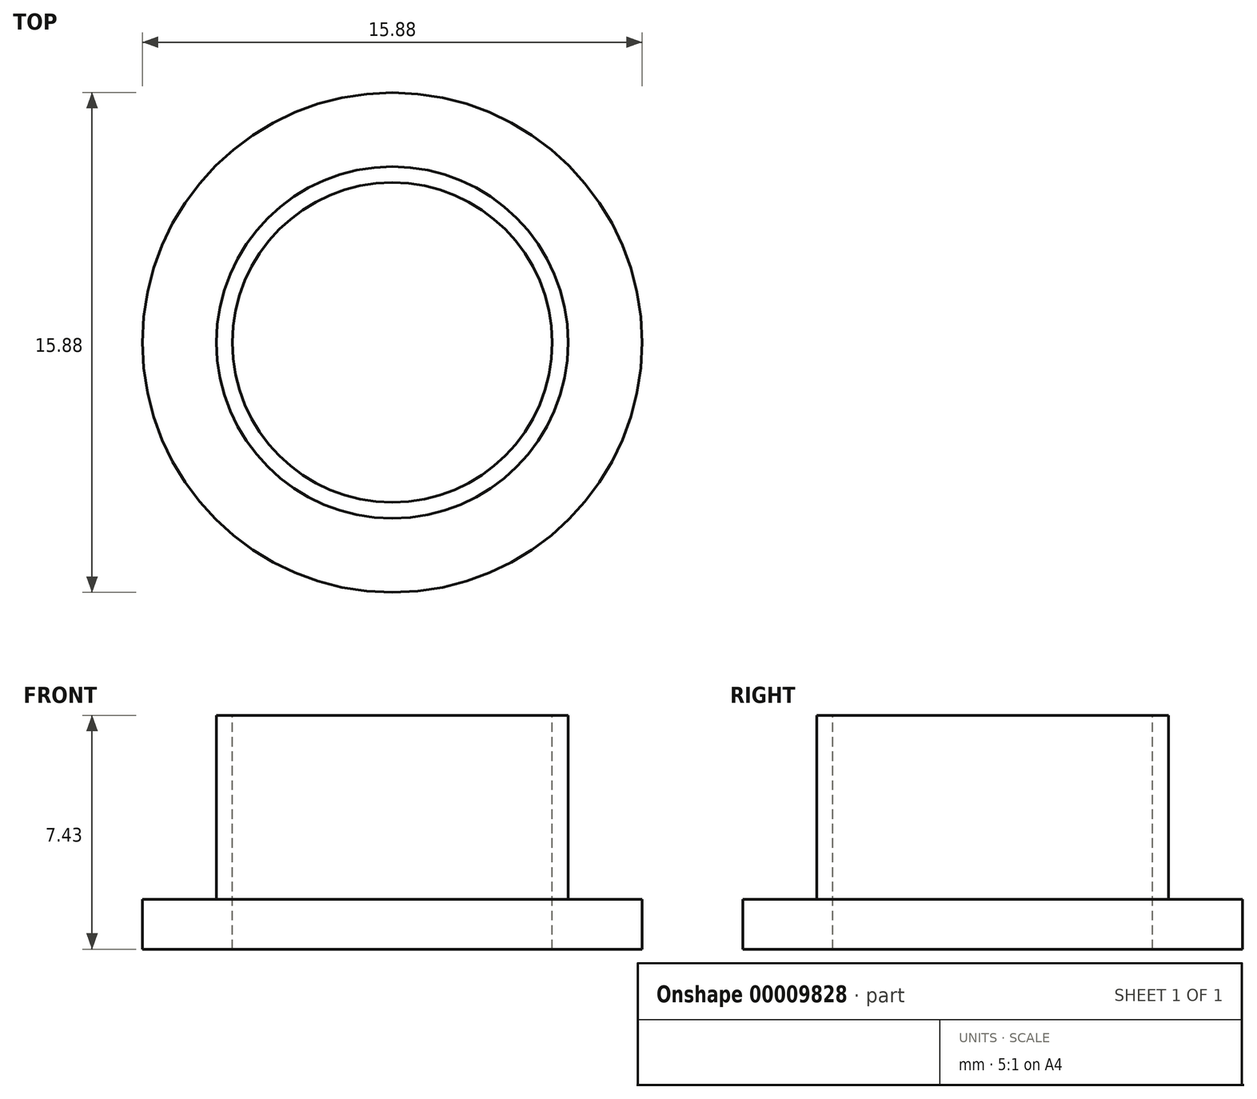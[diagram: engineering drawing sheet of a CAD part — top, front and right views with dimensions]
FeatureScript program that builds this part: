
annotation { "Feature Type Name" : "Feature", "Feature Type Description" : "" }
export const myFeature = defineFeature(function(context is Context, id is Id, definition is map)
    precondition{}
    {
        {
            var Q0;
            Q0=qCreatedBy(makeId("Top.planeOp"),FACE);
            var sketch = newSketch(context, id + "F0", { "sketchPlane" : qUnion([Q0])});
            skCircle(sketch, "E0", {"center": v(0, 0) * mm, "radius": 7.94 * mm});
            skSolve(sketch);
        }
        {
            var Q0;
            Q0=makeQuery(id+"F0.imprint","IMPRINT",FACE,{"disambiguationData":[TD([[makeQuery(id+"F0.imprint","IMPRINT",EDGE,{"derivedFrom":sQuery(id+"F0.wireOp",EDGE,"E0")}),1.0]])]});
            extrude(context, id + "F1", {"entities" : qUnion([Q0]), "depth" : 1.59 * mm});
        }
        {
            var Q0;
            Q0=makeQuery(id+"F1.opExtrude","CAP_FACE",FACE,{"disambiguationData":[OSD([sQuery(id+"F0.wireOp",EDGE,"E0")])],"isStart":false});
            var sketch = newSketch(context, id + "F2", { "sketchPlane" : qUnion([Q0])});
            skCircle(sketch, "E1", {"center": v(0, 0) * mm, "radius": 5.59 * mm});
            skSolve(sketch);
        }
        {
            var Q0;
            Q0=makeQuery(id+"F2.imprint","IMPRINT",FACE,{"disambiguationData":[TD([[makeQuery(id+"F2.imprint","IMPRINT",EDGE,{"derivedFrom":sQuery(id+"F2.wireOp",EDGE,"E1")}),1.0]])]});
            extrude(context, id + "F3", {"entities" : qUnion([Q0]), "operationType" : NewBodyOperationType.ADD, "depth" : 5.84 * mm});
        }
        {
            var Q0;
            Q0=makeQuery(id+"F3.opExtrude","CAP_FACE",FACE,{"disambiguationData":[OSD([sQuery(id+"F2.wireOp",EDGE,"E1")])],"isStart":false});
            var sketch = newSketch(context, id + "F4", { "sketchPlane" : qUnion([Q0])});
            skCircle(sketch, "E2", {"center": v(0, 0) * mm, "radius": 5.08 * mm});
            skSolve(sketch);
        }
        {
            var Q0;
            Q0=makeQuery(id+"F4.imprint","IMPRINT",FACE,{"disambiguationData":[TD([[makeQuery(id+"F4.imprint","IMPRINT",EDGE,{"derivedFrom":sQuery(id+"F4.wireOp",EDGE,"E2")}),1.0]])]});
            var Q1;
            Q1=makeQuery(id+"F1.opExtrude","CAP_FACE",FACE,{"disambiguationData":[OSD([sQuery(id+"F0.wireOp",EDGE,"E0")])],"isStart":true});
            extrude(context, id + "F5", {"entities" : qUnion([Q0]), "operationType" : NewBodyOperationType.REMOVE, "endBound" : BoundingType.UP_TO_SURFACE, "oppositeDirection" : true, "endBoundEntityFace" : qUnion([Q1]), "depth" : 25.4 * mm});
        }
    });
